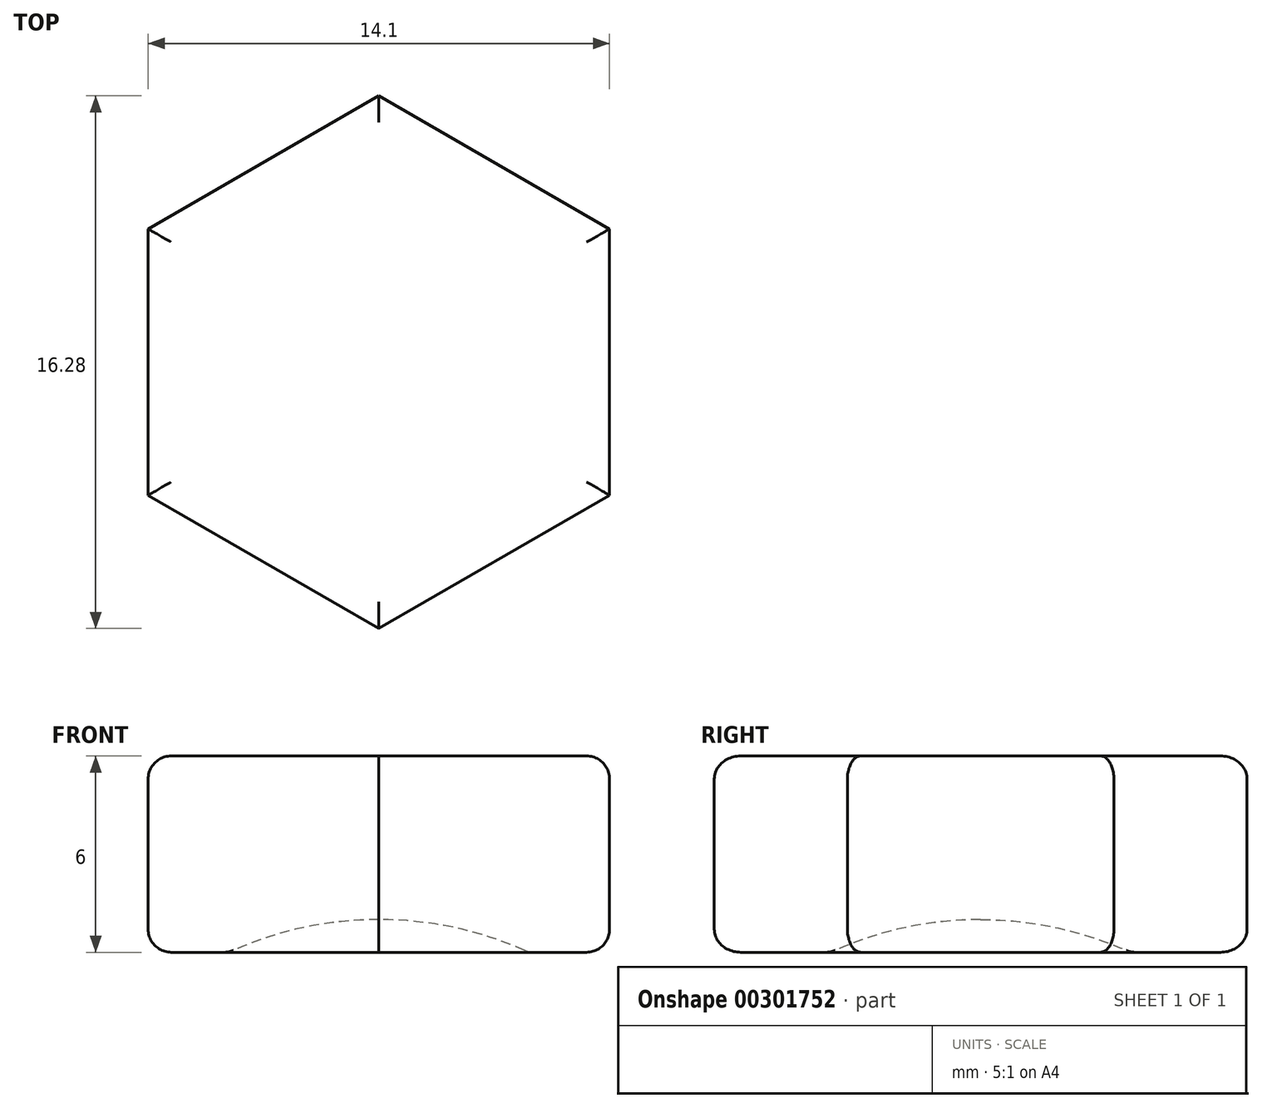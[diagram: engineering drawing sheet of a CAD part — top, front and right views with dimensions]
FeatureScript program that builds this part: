
annotation { "Feature Type Name" : "Feature", "Feature Type Description" : "" }
export const myFeature = defineFeature(function(context is Context, id is Id, definition is map)
    precondition{}
    {
        {
            var Q0;
            Q0=qCreatedBy(makeId("Top.planeOp"),FACE);
            var sketch = newSketch(context, id + "F0", { "sketchPlane" : qUnion([Q0])});
            skCircle(sketch, "E0.cCircle", {"center": v(0, 0) * mm, "radius": 8.14 * mm, "construction": true});
            skLineSegment(sketch, "E0.0", {"start": v(7.05, 4.07) * mm, "end": v(7.05, -4.07) * mm});
            skLineSegment(sketch, "E0.1", {"start": v(7.05, -4.07) * mm, "end": v(0, -8.14) * mm});
            skLineSegment(sketch, "E0.2", {"start": v(0, -8.14) * mm, "end": v(-7.05, -4.07) * mm});
            skLineSegment(sketch, "E0.3", {"start": v(-7.05, -4.07) * mm, "end": v(-7.05, 4.07) * mm});
            skLineSegment(sketch, "E0.4", {"start": v(-7.05, 4.07) * mm, "end": v(0, 8.14) * mm});
            skLineSegment(sketch, "E0.5", {"start": v(0, 8.14) * mm, "end": v(7.05, 4.07) * mm});
            skSolve(sketch);
        }
        {
            var Q0;
            Q0 = qSketchRegion(id + "F0", true);
            extrude(context, id + "F1", {"entities" : qUnion([Q0]), "depth" : 6 * mm});
        }
        {
            var Q0;
            Q0=qCreatedBy(makeId("Right.planeOp"),FACE);
            var sketch = newSketch(context, id + "F2", { "sketchPlane" : qUnion([Q0])});
            skLineSegment(sketch, "E1", {"start": v(0, 0) * mm, "end": v(0, -10) * mm});
            skArc(sketch, "E2", {"start": v(0, 1) * mm, "mid": v(-11, -10) * mm, "end": v(0, -21) * mm});
            skLineSegment(sketch, "E3", {"start": v(0, -10) * mm, "end": v(0, -21) * mm});
            skLineSegment(sketch, "E4", {"start": v(0, 0) * mm, "end": v(0, 1) * mm});
            skSolve(sketch);
        }
        {
            var Q0;
            Q0 = qSketchRegion(id + "F2", true);
            var Q1;
            Q1=sQuery(id+"F2.wireOp",EDGE,"E1");
            revolve(context, id + "F3", {"operationType" : NewBodyOperationType.REMOVE, "entities" : qUnion([Q0]), "axis" : qUnion([Q1]), "revolveType" : RevolveType.FULL, "oppositeDirection" : true});
        }
        {
            var Q0;
            Q0=makeQuery(id+"F1.opExtrude","CAP_FACE",FACE,{"disambiguationData":[OSD([sQuery(id+"F0.wireOp",EDGE,"E0.0"),sQuery(id+"F0.wireOp",EDGE,"E0.1"),sQuery(id+"F0.wireOp",EDGE,"E0.2"),sQuery(id+"F0.wireOp",EDGE,"E0.3"),sQuery(id+"F0.wireOp",EDGE,"E0.4"),sQuery(id+"F0.wireOp",EDGE,"E0.5")])],"isStart":false});
            var Q1;
            Q1=makeQuery(id+"F1.opExtrude","CAP_FACE",FACE,{"disambiguationData":[OSD([sQuery(id+"F0.wireOp",EDGE,"E0.0"),sQuery(id+"F0.wireOp",EDGE,"E0.1"),sQuery(id+"F0.wireOp",EDGE,"E0.2"),sQuery(id+"F0.wireOp",EDGE,"E0.3"),sQuery(id+"F0.wireOp",EDGE,"E0.4"),sQuery(id+"F0.wireOp",EDGE,"E0.5")])],"isStart":true});
            fillet(context, id + "F4", {"entities" : qUnion([Q0, Q1]), "radius" : 0.7 * mm, "tangentPropagation" : true, "allowEdgeOverflow" : false});
        }
    });
